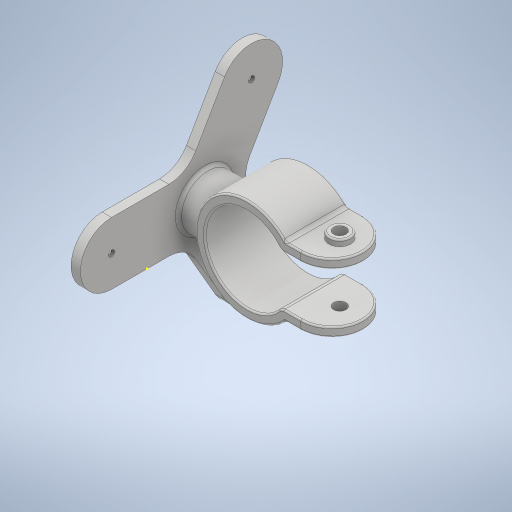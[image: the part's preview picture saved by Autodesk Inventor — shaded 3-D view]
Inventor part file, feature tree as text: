
AUTODESK INVENTOR PART (.ipt)
format: ipt  version: 2023 (Build 270158000, 158)  size: 492,032 bytes
history: native  units: mm
features: sketch x7, fillet x6, extrude x5, hole x4, plane x1
ambient origin geometry x8: Origin, YZ Plane, XZ Plane, XY Plane, X Axis, Y Axis, Z Axis, Center Point
bodies: 实体1 (feature_tree)
feature tree (23):
  extrude  "拉伸1"  Depth=20.0mm
  extrude  "拉伸2"  Depth=3.0mm TaperAngle=0.0deg
  sketch  "草图3"  dims[d0=20.0mm d3=20.0mm]
  sketch  "草图4"  dims[d4=20.0mm d6=3.0mm d7=0.0mm]
  sketch  "草图5"  dims[d9=10.0mm d10=0.0mm d27=20.0mm d28=0.0mm d29=1.0mm]
  plane  "工作平面1"
  extrude  "拉伸4"  Depth=10.0mm TaperAngle=0.0deg
  fillet  "圆角1"  Radius=1.0mm
  fillet  "圆角2"  Radius=20.594885mm
  fillet  "圆角3"  Radius=0.5mm
  hole  "孔1"  [1 undecoded]
  fillet  "圆角4"  Radius=10.0mm
  hole  "孔2"  [1 undecoded]
  hole  "孔3"  [1 undecoded]
  hole  "孔4"  [1 undecoded]
  sketch  "草图7"  dims[d40=7.421mm d41=10.0mm]
  extrude  "拉伸5"  Depth=10.0mm
  fillet  "圆角5"  Radius=1.0mm
  fillet  "圆角6"  Radius=12.0mm
  extrude  "拉伸6"  Depth=10.0mm
  sketch  "草图6"  dims[d30=10.0mm d31=7.5mm d32=4.0mm d33=6.0mm d34=4.0mm d35=2.0mm d36=90.0deg d37=0.5mm d38=20.594885mm d39=0.5mm]
  sketch  "草图8"  dims[d42=1.941mm d43=5.029mm d44=4.0mm d45=2.0mm d46=90.0deg d47=7.675mm d48=20.594885mm d49=10.0mm d50=10.0mm]
  sketch  "草图11"  dims[d51=1.941mm d52=5.029mm d53=4.0mm d54=2.0mm d55=90.0deg d56=7.675mm d57=20.594885mm d58=10.0mm d59=10.0mm d60=1.941mm d61=5.029mm d62=4.0mm d63=2.0mm d64=90.0deg d65=7.675mm d66=20.594885mm d67=7.0mm d68=2.0mm d69=0.0mm d70=0.5mm d71=2.0mm d72=1.0mm d73=0.0mm d74=12.0mm d75=12.0mm d76=12.0mm d77=2.0mm d78=0.0mm]
note: 4 required parameter values undecoded (feature->parameter linkage not recoverable at this tier; creation-order binding heuristic only, values carry confidence <= 0.55)
